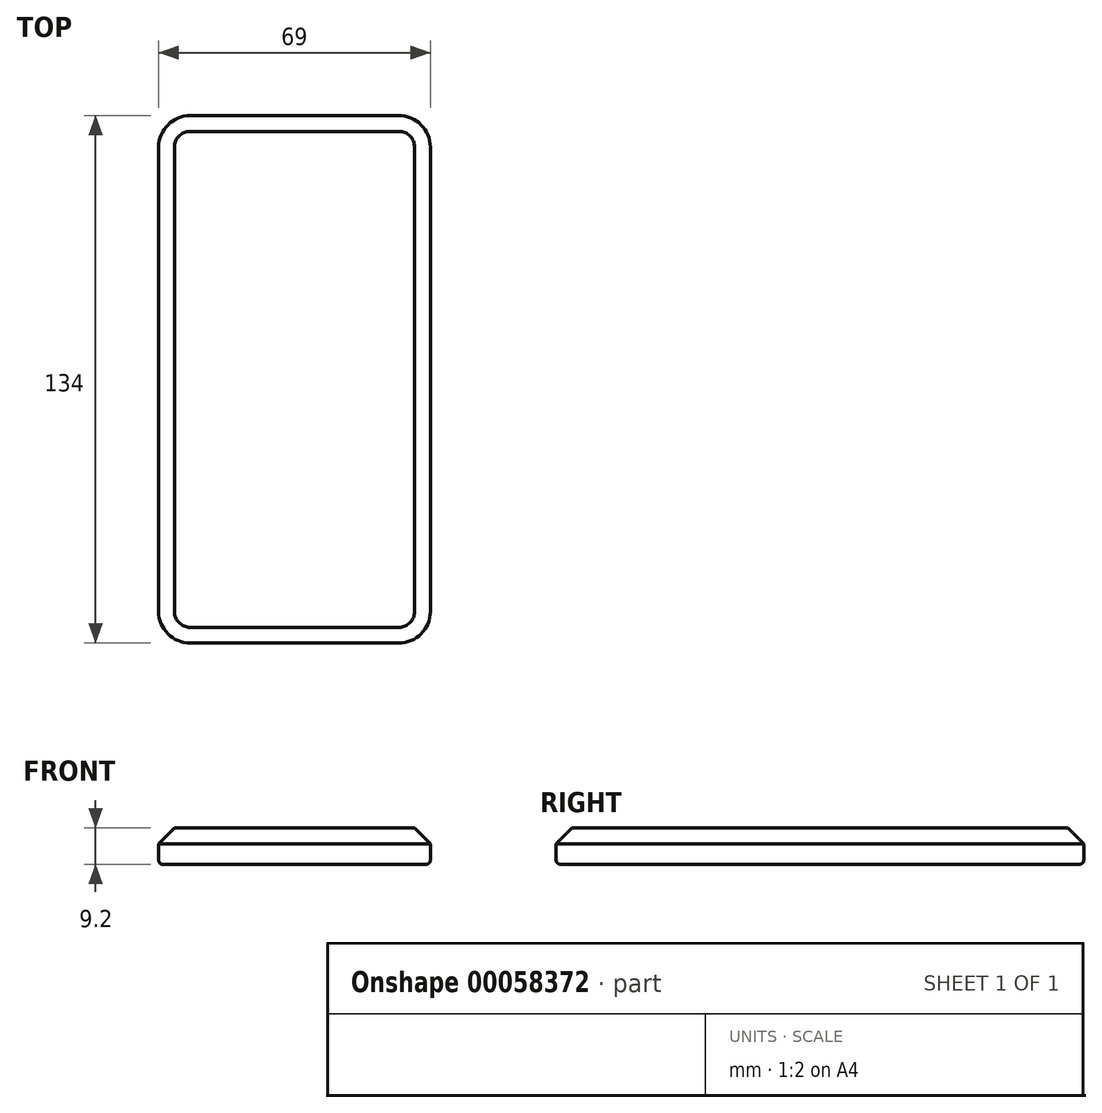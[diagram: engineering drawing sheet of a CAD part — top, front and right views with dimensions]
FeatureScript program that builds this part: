
annotation { "Feature Type Name" : "Feature", "Feature Type Description" : "" }
export const myFeature = defineFeature(function(context is Context, id is Id, definition is map)
    precondition{}
    {
        {
            var Q0;
            Q0=qCreatedBy(makeId("Top.planeOp"),FACE);
            var sketch = newSketch(context, id + "F0", { "sketchPlane" : qUnion([Q0])});
            skLineSegment(sketch, "E0.bottom", {"start": v(-26.5, 67) * mm, "end": v(26.5, 67) * mm});
            skLineSegment(sketch, "E0.top", {"start": v(-26.5, -67) * mm, "end": v(26.5, -67) * mm});
            skLineSegment(sketch, "E0.left", {"start": v(-34.5, 59) * mm, "end": v(-34.5, -59) * mm});
            skLineSegment(sketch, "E0.right", {"start": v(34.5, 59) * mm, "end": v(34.5, -59) * mm});
            skPoint(sketch, "E1.visualSharp", {"position": v(-34.5, 67) * mm});
            skArc(sketch, "E1.filletArc", {"start": v(-26.5, 67) * mm, "mid": v(-32.16, 64.66) * mm, "end": v(-34.5, 59) * mm});
            skPoint(sketch, "E2.visualSharp", {"position": v(34.5, 67) * mm});
            skArc(sketch, "E2.filletArc", {"start": v(34.5, 59) * mm, "mid": v(32.16, 64.66) * mm, "end": v(26.5, 67) * mm});
            skPoint(sketch, "E3.visualSharp", {"position": v(34.5, -67) * mm});
            skArc(sketch, "E3.filletArc", {"start": v(26.5, -67) * mm, "mid": v(32.16, -64.66) * mm, "end": v(34.5, -59) * mm});
            skPoint(sketch, "E4.visualSharp", {"position": v(-34.5, -67) * mm});
            skArc(sketch, "E4.filletArc", {"start": v(-34.5, -59) * mm, "mid": v(-32.16, -64.66) * mm, "end": v(-26.5, -67) * mm});
            skSolve(sketch);
        }
        {
            var Q0;
            Q0 = qSketchRegion(id + "F0", true);
            extrude(context, id + "F1", {"entities" : qUnion([Q0]), "depth" : 9.2 * mm});
        }
        {
            var Q0;
            Q0=makeQuery(id+"F1.opExtrude","CAP_EDGE",EDGE,{"disambiguationData":[OSD([sQuery(id+"F0.wireOp",EDGE,"E0.left")])],"isStart":false});
            chamfer(context, id + "F2", {"entities" : qUnion([Q0]), "width" : 4 * mm, "tangentPropagation" : true});
        }
        {
            var Q0;
            Q0=makeQuery(id+"F1.opExtrude","CAP_EDGE",EDGE,{"disambiguationData":[OSD([sQuery(id+"F0.wireOp",EDGE,"E0.right")])],"isStart":true});
            fillet(context, id + "F3", {"entities" : qUnion([Q0]), "radius" : 1 * mm, "tangentPropagation" : true, "allowEdgeOverflow" : false});
        }
    });
